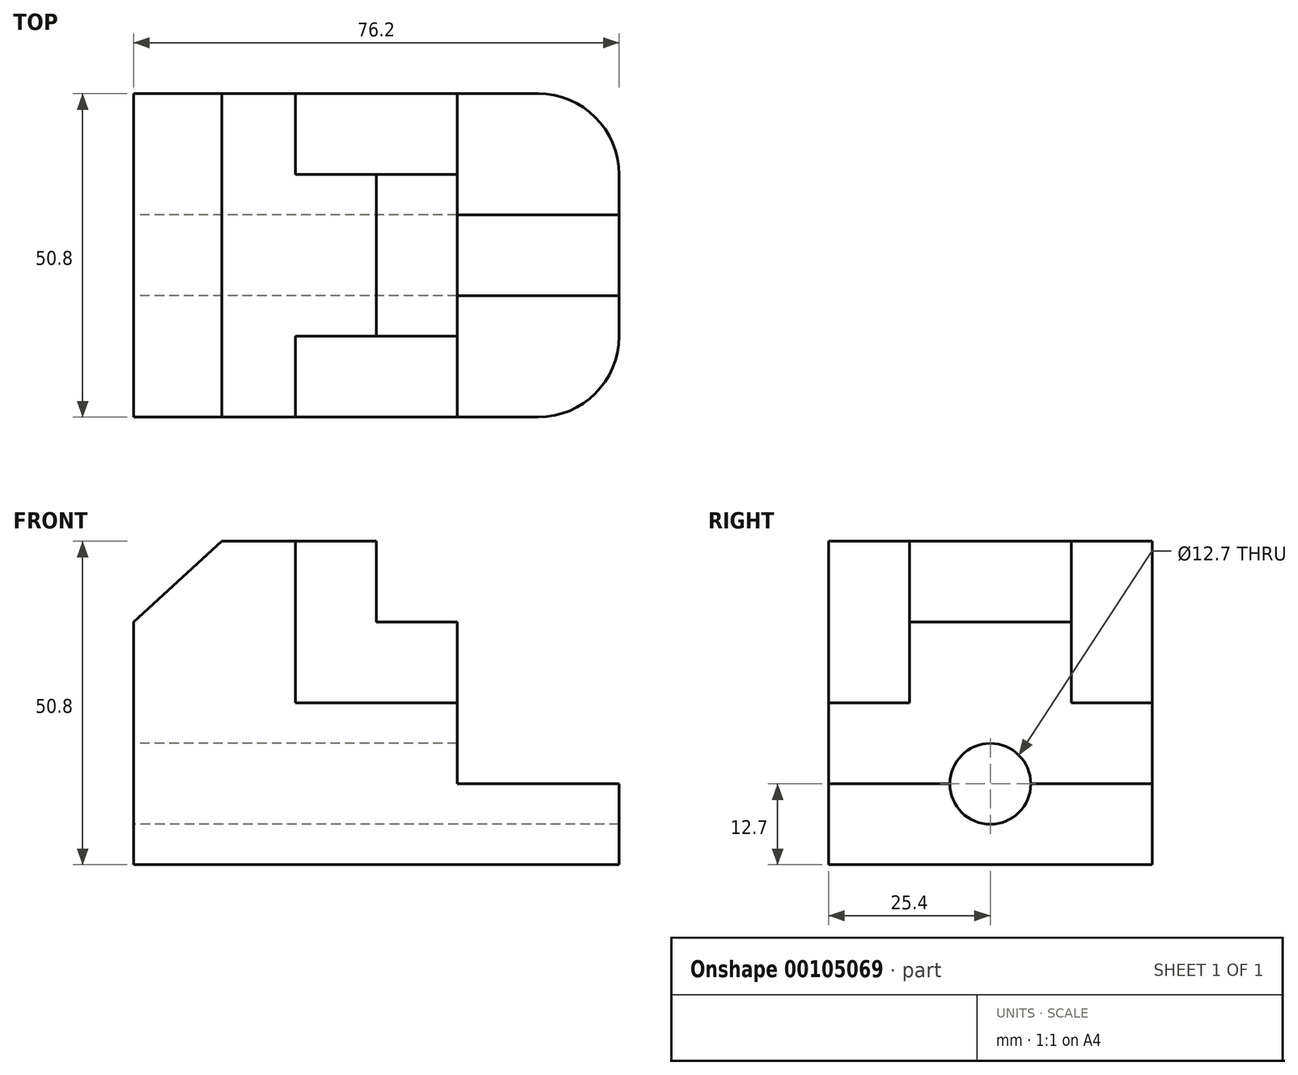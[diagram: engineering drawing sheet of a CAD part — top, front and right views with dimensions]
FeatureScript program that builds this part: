
annotation { "Feature Type Name" : "Feature", "Feature Type Description" : "" }
export const myFeature = defineFeature(function(context is Context, id is Id, definition is map)
    precondition{}
    {
        {
            var Q0;
            Q0=qCreatedBy(makeId("Front.planeOp"),FACE);
            var sketch = newSketch(context, id + "F0", { "sketchPlane" : qUnion([Q0])});
            skLineSegment(sketch, "E0", {"start": v(0, 0) * mm, "end": v(0, 38.1) * mm});
            skLineSegment(sketch, "E1", {"start": v(0, 38.1) * mm, "end": v(13.83, 50.8) * mm});
            skLineSegment(sketch, "E2", {"start": v(13.83, 50.8) * mm, "end": v(25.4, 50.8) * mm});
            skLineSegment(sketch, "E3", {"start": v(25.4, 50.8) * mm, "end": v(25.4, 25.4) * mm});
            skLineSegment(sketch, "E4", {"start": v(25.4, 25.4) * mm, "end": v(50.8, 25.4) * mm});
            skLineSegment(sketch, "E5", {"start": v(50.8, 25.4) * mm, "end": v(50.8, 12.7) * mm});
            skLineSegment(sketch, "E6", {"start": v(50.8, 12.7) * mm, "end": v(76.2, 12.7) * mm});
            skLineSegment(sketch, "E7", {"start": v(76.2, 12.7) * mm, "end": v(76.2, 0) * mm});
            skLineSegment(sketch, "E8", {"start": v(76.2, 0) * mm, "end": v(0, 0) * mm});
            skLineSegment(sketch, "E9", {"start": v(25.4, 50.8) * mm, "end": v(38.1, 50.8) * mm});
            skLineSegment(sketch, "E10", {"start": v(50.8, 38.1) * mm, "end": v(50.8, 25.4) * mm});
            skLineSegment(sketch, "E11.top", {"start": v(50.8, 38.1) * mm, "end": v(38.1, 38.1) * mm});
            skLineSegment(sketch, "E11.right", {"start": v(38.1, 50.8) * mm, "end": v(38.1, 38.1) * mm});
            skSolve(sketch);
        }
        {
            var Q0;
            Q0=makeQuery(id+"F0.imprint","IMPRINT",FACE,{"disambiguationData":[TD([[makeQuery(id+"F0.imprint","IMPRINT",EDGE,{"derivedFrom":sQuery(id+"F0.wireOp",EDGE,"E0")}),-1.0]])]});
            extrude(context, id + "F1", {"entities" : qUnion([Q0]), "endBound" : BoundingType.SYMMETRIC, "depth" : 50.8 * mm});
        }
        {
            var Q0;
            Q0=makeQuery(id+"F0.imprint","IMPRINT",FACE,{"disambiguationData":[TD([[makeQuery(id+"F0.imprint","IMPRINT",EDGE,{"derivedFrom":sQuery(id+"F0.wireOp",EDGE,"E3")}),1.0]])]});
            extrude(context, id + "F2", {"entities" : qUnion([Q0]), "operationType" : NewBodyOperationType.ADD, "endBound" : BoundingType.SYMMETRIC, "depth" : 25.4 * mm});
        }
        {
            var Q0;
            Q0=makeQuery(id+"F1.opExtrude","SWEPT_FACE",FACE,{"disambiguationData":[OSD([sQuery(id+"F0.wireOp",EDGE,"E0")])]});
            var sketch = newSketch(context, id + "F3", { "sketchPlane" : qUnion([Q0])});
            skCircle(sketch, "E12", {"center": v(0, 12.7) * mm, "radius": 6.35 * mm});
            skSolve(sketch);
        }
        {
            var Q0;
            Q0=makeQuery(id+"F3.imprint","IMPRINT",FACE,{"disambiguationData":[TD([[makeQuery(id+"F3.imprint","IMPRINT",EDGE,{"derivedFrom":sQuery(id+"F3.wireOp",EDGE,"E12")}),1.0]])]});
            extrude(context, id + "F4", {"entities" : qUnion([Q0]), "operationType" : NewBodyOperationType.REMOVE, "endBound" : BoundingType.THROUGH_ALL, "oppositeDirection" : true, "depth" : 25.4 * mm});
        }
        {
            var Q0;
            Q0=makeQuery(id+"F1.opExtrude","CAP_EDGE",EDGE,{"disambiguationData":[OSD([sQuery(id+"F0.wireOp",EDGE,"E7")])],"isStart":true});
            var Q1;
            Q1=makeQuery(id+"F1.opExtrude","CAP_EDGE",EDGE,{"disambiguationData":[OSD([sQuery(id+"F0.wireOp",EDGE,"E7")])],"isStart":false});
            fillet(context, id + "F5", {"entities" : qUnion([Q0, Q1]), "radius" : 12.7 * mm, "tangentPropagation" : true, "allowEdgeOverflow" : false});
        }
    });
